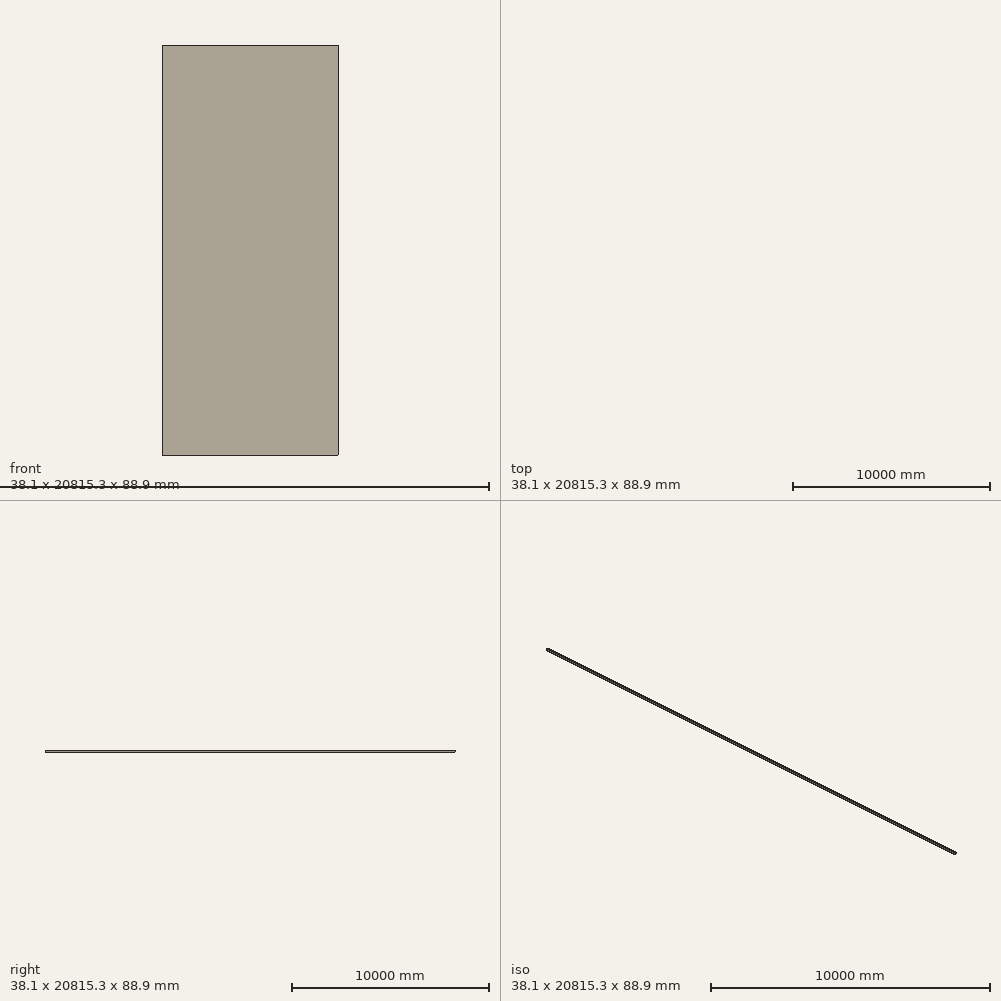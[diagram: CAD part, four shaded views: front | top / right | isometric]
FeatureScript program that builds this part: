
annotation { "Feature Type Name" : "Feature", "Feature Type Description" : "" }
export const myFeature = defineFeature(function(context is Context, id is Id, definition is map)
    precondition{}
    {
        {
            var Q0;
            Q0=qCreatedBy(makeId("Front.planeOp"),FACE);
            var sketch = newSketch(context, id + "F0", { "sketchPlane" : qUnion([Q0])});
            skLineSegment(sketch, "E0.bottom", {"start": v(0, 0) * mm, "end": v(38.1, 0) * mm});
            skLineSegment(sketch, "E0.top", {"start": v(0, 88.9) * mm, "end": v(38.1, 88.9) * mm});
            skLineSegment(sketch, "E0.left", {"start": v(0, 0) * mm, "end": v(0, 88.9) * mm});
            skLineSegment(sketch, "E0.right", {"start": v(38.1, 0) * mm, "end": v(38.1, 88.9) * mm});
            skSolve(sketch);
        }
        {
            var Q0;
            Q0 = qSketchRegion(id + "F0", true);
            extrude(context, id + "F1", {"entities" : qUnion([Q0]), "depth" : 20815.3 * mm, "offsetDistance" : 25.4 * mm});
        }
    });
